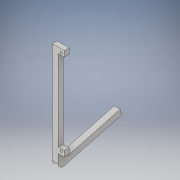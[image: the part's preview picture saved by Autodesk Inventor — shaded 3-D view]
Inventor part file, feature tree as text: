
AUTODESK INVENTOR PART (.ipt)
format: ipt  version: 2018 (Build 220112000, 112)  size: 142,848 bytes
history: native  units: in
note: dims shown in document units (in); Inventor stores cm internally (conversion verified against a paired STEP export)
features: extrude x2, sketch x1
ambient origin geometry x8: Origin, YZ Plane, XZ Plane, XY Plane, X Axis, Y Axis, Z Axis, Center Point
bodies: Body1 (feature_tree)
feature tree (3):
  extrude  "Extrusion3"  Depth=0.315in
  extrude  "Extrusion4"  Depth=0.315in
  sketch  "Sketch1"  dims[d0=4.8925in d1=0.315in d2=0.122in d3=0.122in d4=4.526in d5=0.1181in d6=3.0886in d7=0.315in d17=0.2559in d18=0.0in d19=0.4724in d20=75.0deg d21=0.315in d22=3.1496in d23=0.2756in d24=0.0in]
